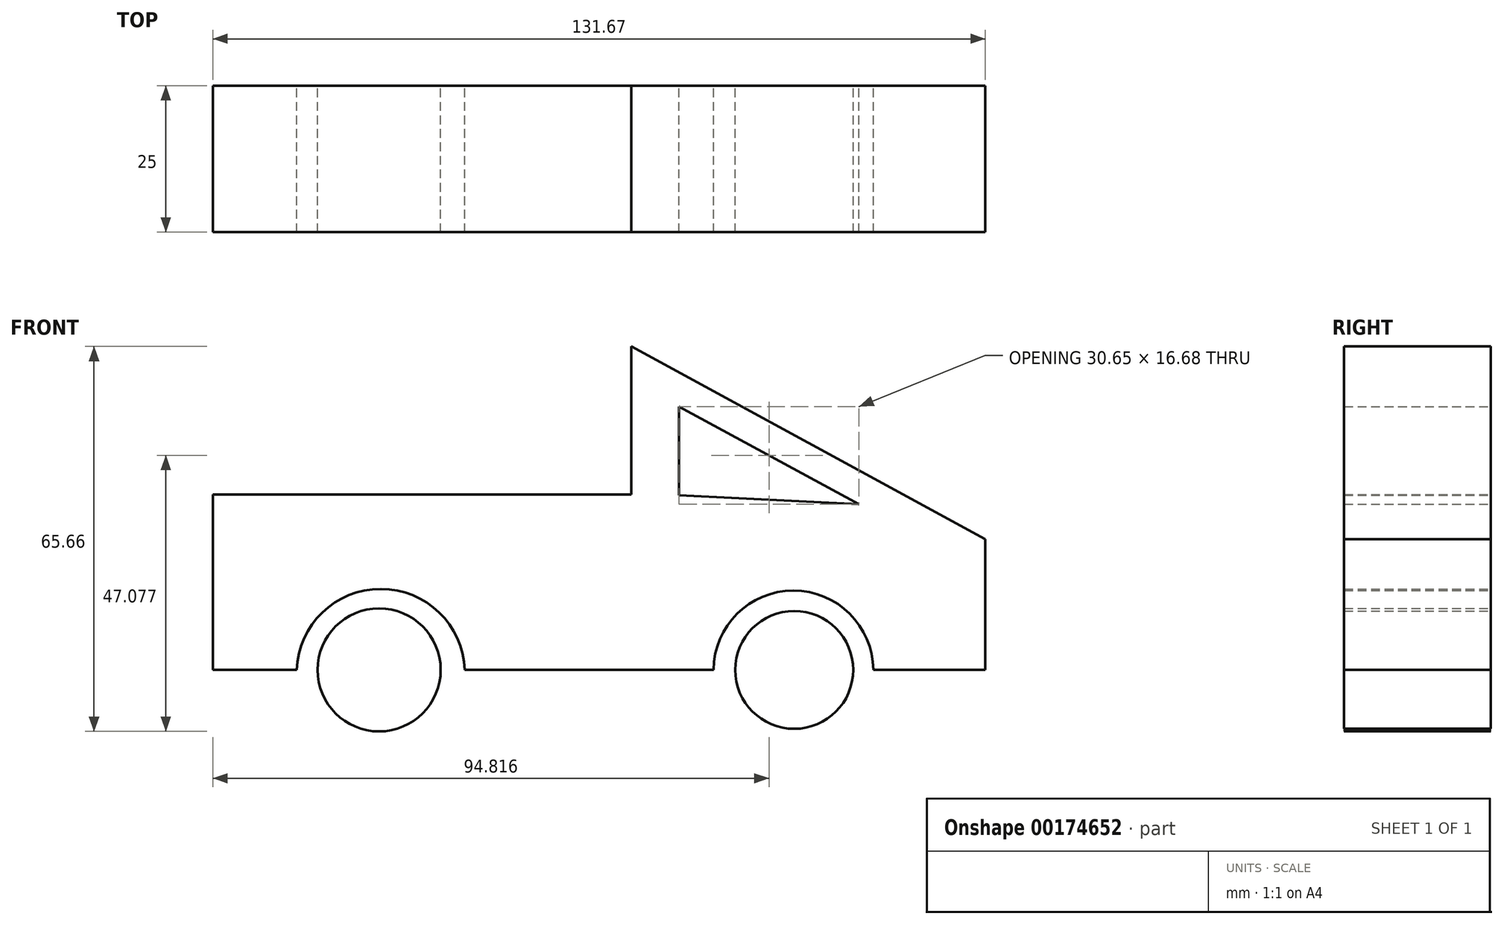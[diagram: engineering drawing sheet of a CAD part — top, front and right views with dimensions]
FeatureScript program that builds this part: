
annotation { "Feature Type Name" : "Feature", "Feature Type Description" : "" }
export const myFeature = defineFeature(function(context is Context, id is Id, definition is map)
    precondition{}
    {
        {
            var Q0;
            Q0=qCreatedBy(makeId("Front.planeOp"),FACE);
            var sketch = newSketch(context, id + "F0", { "sketchPlane" : qUnion([Q0])});
            skCircle(sketch, "E0", {"center": v(-42.95, 0) * mm, "radius": 10.5 * mm});
            skCircle(sketch, "E1", {"center": v(27.8, 0) * mm, "radius": 10.05 * mm});
            skLineSegment(sketch, "E2", {"start": v(-71.31, 0) * mm, "end": v(-71.31, 29.9) * mm});
            skLineSegment(sketch, "E3", {"start": v(-71.31, 0) * mm, "end": v(-57, 0) * mm});
            skArc(sketch, "E4", {"start": v(-28.36, 0) * mm, "mid": v(-42.67, 13.82) * mm, "end": v(-57, 0) * mm});
            skLineSegment(sketch, "E5", {"start": v(-28.36, 0) * mm, "end": v(14.04, 0) * mm});
            skArc(sketch, "E6", {"start": v(41.27, 0) * mm, "mid": v(27.65, 13.53) * mm, "end": v(14.04, 0) * mm});
            skLineSegment(sketch, "E7", {"start": v(-71.31, 29.9) * mm, "end": v(0, 29.9) * mm});
            skLineSegment(sketch, "E8", {"start": v(0, 29.9) * mm, "end": v(0, 55.17) * mm});
            skLineSegment(sketch, "E9", {"start": v(0, 55.17) * mm, "end": v(60.36, 22.32) * mm});
            skLineSegment(sketch, "E10", {"start": v(60.36, 22.32) * mm, "end": v(60.36, 0) * mm});
            skLineSegment(sketch, "E11", {"start": v(41.27, 0) * mm, "end": v(60.36, 0) * mm});
            skPoint(sketch, "E12.orphan", {"position": v(60.36, -2.1) * mm});
            skLineSegment(sketch, "E13", {"start": v(8.18, 44.93) * mm, "end": v(8.18, 29.77) * mm});
            skLineSegment(sketch, "E14", {"start": v(8.18, 44.93) * mm, "end": v(38.83, 28.25) * mm});
            skLineSegment(sketch, "E15", {"start": v(8.18, 29.77) * mm, "end": v(38.83, 28.25) * mm});
            skSolve(sketch);
        }
        {
            var Q0;
            Q0 = qSketchRegion(id + "F0", true);
            extrude(context, id + "F1", {"entities" : qUnion([Q0]), "depth" : 25 * mm});
        }
    });
